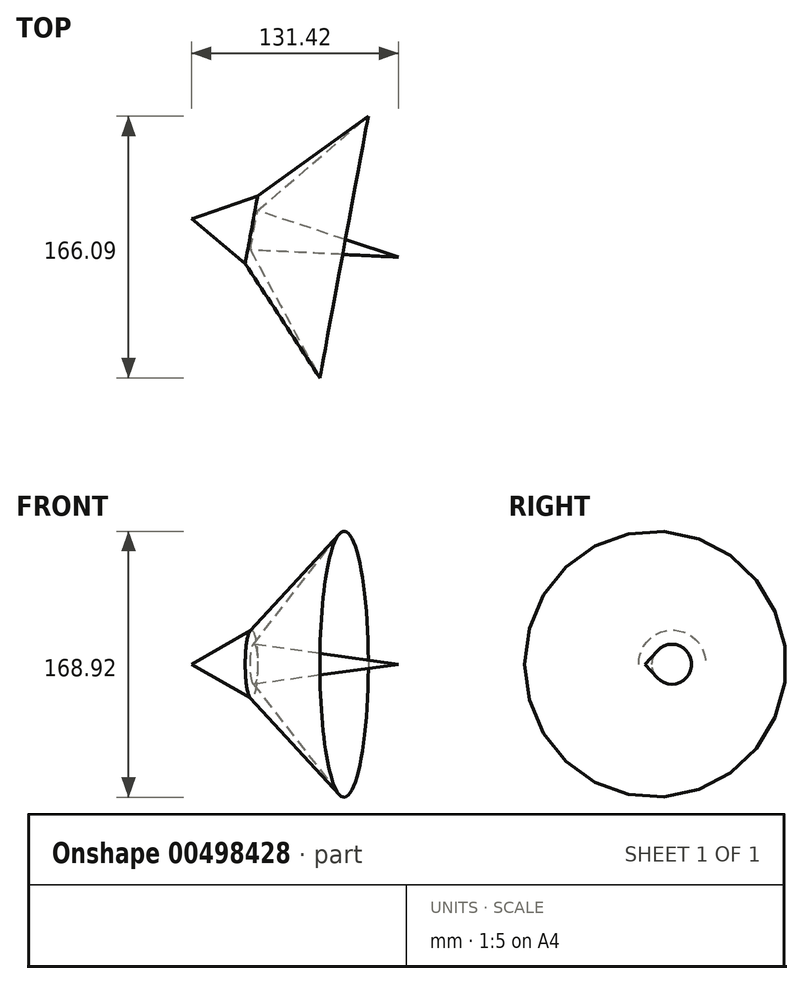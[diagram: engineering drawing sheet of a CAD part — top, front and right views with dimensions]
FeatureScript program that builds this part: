
annotation { "Feature Type Name" : "Feature", "Feature Type Description" : "" }
export const myFeature = defineFeature(function(context is Context, id is Id, definition is map)
    precondition{}
    {
        {
            var Q0;
            Q0=qCreatedBy(makeId("Top.planeOp"),FACE);
            var sketch = newSketch(context, id + "F0", { "sketchPlane" : qUnion([Q0])});
            skLineSegment(sketch, "E0", {"start": v(-70.58, -14) * mm, "end": v(-28.6, 0.3) * mm});
            skLineSegment(sketch, "E1", {"start": v(-28.6, 0.3) * mm, "end": v(41.68, 51.1) * mm});
            skLineSegment(sketch, "E2", {"start": v(41.68, 51.1) * mm, "end": v(-28.6, -8.82) * mm});
            skLineSegment(sketch, "E3", {"start": v(-28.6, -8.82) * mm, "end": v(60.84, -38.33) * mm});
            skLineSegment(sketch, "E4", {"start": v(-70.58, -14) * mm, "end": v(60.84, -38.33) * mm});
            skSolve(sketch);
        }
        {
            var Q0;
            Q0 = qSketchRegion(id + "F0", true);
            var Q1;
            Q1=sQuery(id+"F0.wireOp",EDGE,"E4");
            revolve(context, id + "F1", {"entities" : qUnion([Q0]), "axis" : qUnion([Q1]), "revolveType" : RevolveType.FULL});
        }
    });
